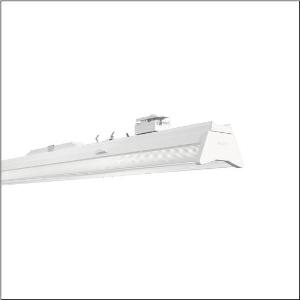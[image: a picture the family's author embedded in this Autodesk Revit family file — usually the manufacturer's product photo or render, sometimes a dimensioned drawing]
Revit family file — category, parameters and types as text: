
# Revit family: licross_r__21_performance_mo_52tm16dn46xg_f566
name_source: partatom
category: Lighting Fixtures
units: mm (PartAtom-declared; Revit-internal decimal feet)

## family parameters
Cut with Voids When Loaded = No
Host = Face
Light Source = No
Part Type = Normal
Room Calculation Point = No
Round Connector Dimension = Use Diameter
Shared = No

## types (1)
- --- (1 x LED, 6000 lm, 32.7 W, 4000K)
    Apparent Load = 33 VA
    CIE Flux Codes = 66 88 96 79 100
    Color Rendering = 80
    Color Temperature = 4000K
    Default Elevation = 1800 mm
    Description = Licross® 21 Performance MO, luminaire insert, of sheet steel, galvanised, coil coated, white, length: 1.500mm, width: 120mm, height: 123mm, LED rated luminous flux: 6.000lm, light colour: 840, control gear: DALI 2, with plug, 5-pole, with phase selection, mains connection: 220..240V, AC, 50/60Hz, rated input power: 33W, halogen-free wiring, primary light control with lens, of plastic, primary optical cover: cover, of PMMA, light emission: direct/indirect distribution, primary light characteristic: symmetric, protection rating (complete): IP40, insulation class (complete): insulation class I (protective earthing), certification: CE, ENEC, UKCA, protection symbol: D if used in an environment without relevant dust loads with corresponding accessories, impact resistance: IK06, permissible ambient temperature for indoor applications: -25..+45°C, corresponds to IFS (International Featured Standards) requirements for safety and quality in the food industry, reducing of maximum allowable ambient temperature of 5°C with ceiling mounting, LABS conformity tested according to VDMA 24364:2018-05, packaging unit: 1 piece
    Height = 114 mm
    Lamp = 1 x LED
    Lamp Light Flux = 6000 lm
    Lamp Power = 32.7 W
    Lamp count = 1
    Length = 1500 mm
    Luminous efficacy = 183 lm/W
    Manufacturer = Siteco
    ModVariant = No
    Model = 52TM16DN46XG
    Mounting Place = Ceiling
    Mounting Type = Pendant
    Number of Poles = 1
    OnlyDefault = Yes
    Power Factor = 1
    Product Name = Licross® 21 Performance MO
    Product group = luminaire insert
    ProductGroupID = 901
    Protection Class = Protection class I
    Protection Degree = IP 40
    RLX_Detail_Level = 1
    RLX_Emergency_Light_Flux = 0 lm
    RLX_Emergency_Type = 0
    RLX_Emergency_Type_DB = No
    RlxData = <blob elided: 33653 chars, md5=b89c573a>
    Socket = socket
    Standby Power = 0 W
    System Light Flux = 6000 lm
    System Power = 33 W
    Type Comments = factory setting: luminous flux: 100 % | dim-lin: 254 | 222 mA
    Type Image = l_1256138.jpg
    URL = http://relux.com
    VarID = @adj_060879
    Voltage = 0 V
    Weight = 0.00 kg
    Width = 120 mm

## geometry (parser evidence)
native form markers: Blend x4, Sweep x12
no freeform markers — native parametric forms only
